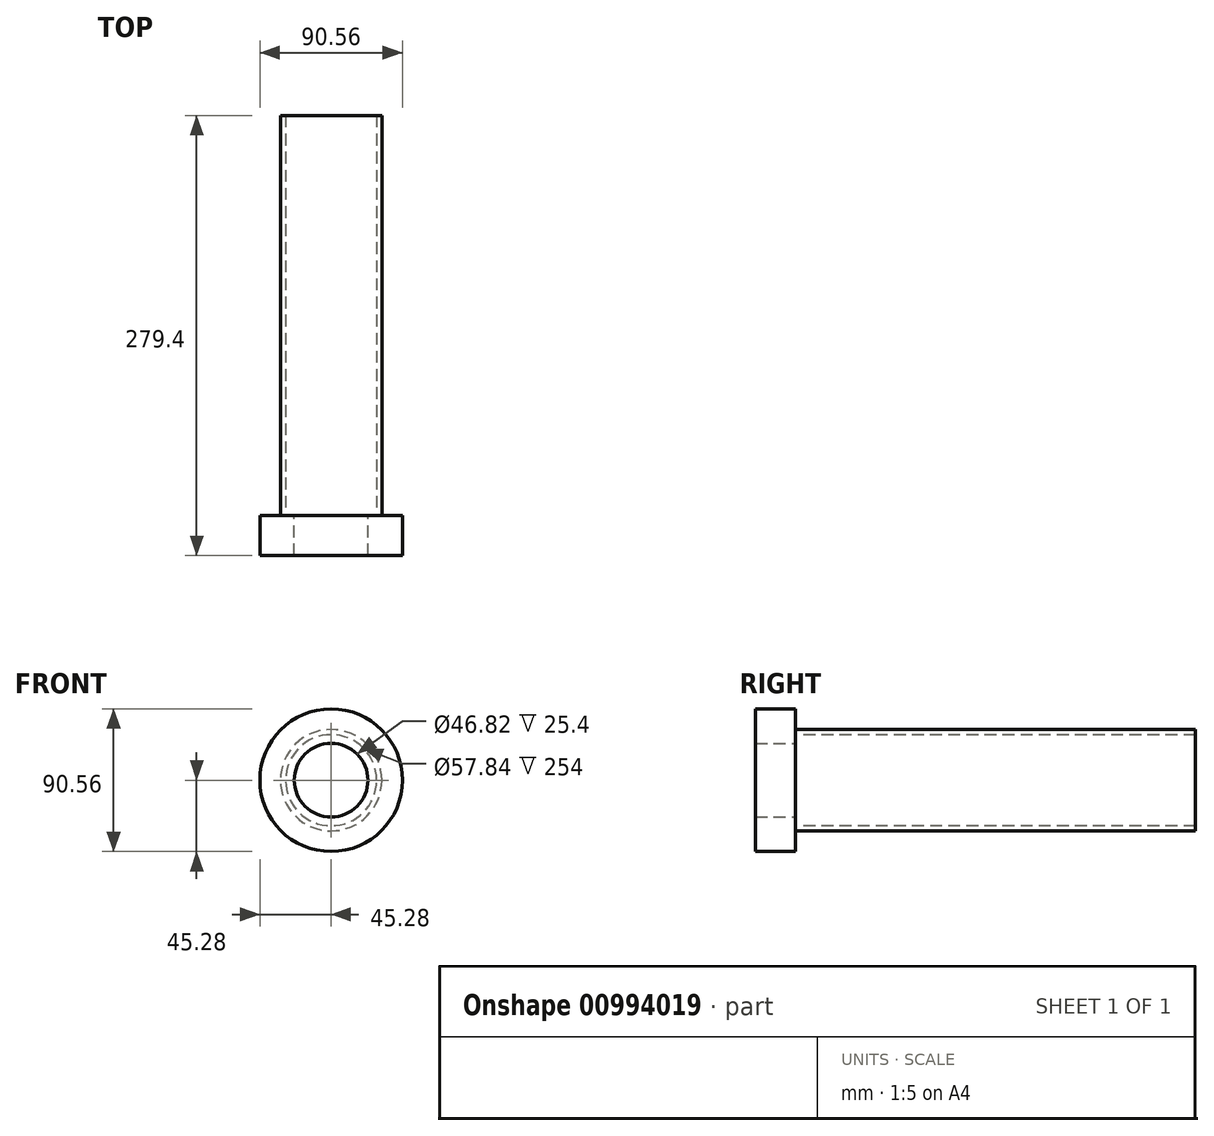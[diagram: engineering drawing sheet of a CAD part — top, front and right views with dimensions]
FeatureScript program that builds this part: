
annotation { "Feature Type Name" : "Feature", "Feature Type Description" : "" }
export const myFeature = defineFeature(function(context is Context, id is Id, definition is map)
    precondition{}
    {
        {
            var Q0;
            Q0=qCreatedBy(makeId("Front.planeOp"),FACE);
            var sketch = newSketch(context, id + "F0", { "sketchPlane" : qUnion([Q0])});
            skCircle(sketch, "E0", {"center": v(0, 0) * mm, "radius": 45.28 * mm});
            skCircle(sketch, "E1", {"center": v(0, 0) * mm, "radius": 23.41 * mm});
            skSolve(sketch);
        }
        {
            var Q0;
            Q0=makeQuery(id+"F0.imprint","IMPRINT",FACE,{"disambiguationData":[TD([[makeQuery(id+"F0.imprint","IMPRINT",EDGE,{"derivedFrom":sQuery(id+"F0.wireOp",EDGE,"E0")}),1.0]])]});
            extrude(context, id + "F1", {"entities" : qUnion([Q0]), "depth" : 25.4 * mm, "offsetDistance" : 25.4 * mm});
        }
        {
            var Q0;
            Q0=makeQuery(id+"F1.opExtrude","CAP_FACE",FACE,{"disambiguationData":[OSD([sQuery(id+"F0.wireOp",EDGE,"E0"),sQuery(id+"F0.wireOp",EDGE,"E1")])],"isStart":true});
            var sketch = newSketch(context, id + "F2", { "sketchPlane" : qUnion([Q0])});
            skCircle(sketch, "E2", {"center": v(0, 0) * mm, "radius": 28.92 * mm});
            skCircle(sketch, "E3", {"center": v(0, 0) * mm, "radius": 32.2 * mm});
            skSolve(sketch);
        }
        {
            var Q0;
            Q0=makeQuery(id+"F2.imprint","IMPRINT",FACE,{"disambiguationData":[TD([[makeQuery(id+"F2.imprint","IMPRINT",EDGE,{"derivedFrom":sQuery(id+"F2.wireOp",EDGE,"E2")}),-1.0]])]});
            extrude(context, id + "F3", {"entities" : qUnion([Q0]), "operationType" : NewBodyOperationType.ADD, "depth" : 254 * mm, "offsetDistance" : 25.4 * mm});
        }
    });
